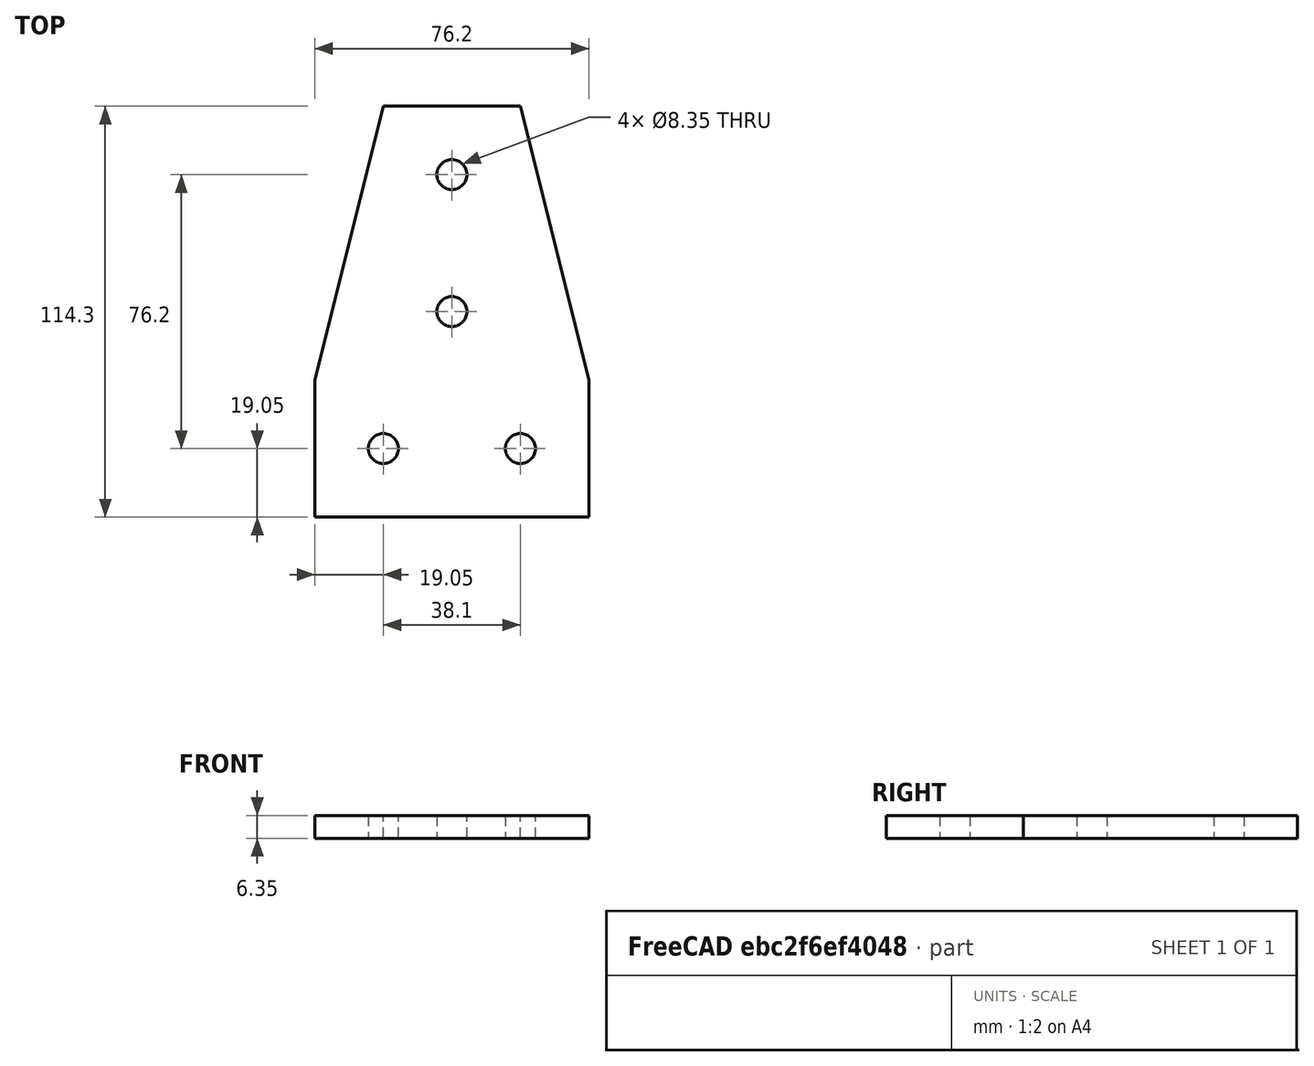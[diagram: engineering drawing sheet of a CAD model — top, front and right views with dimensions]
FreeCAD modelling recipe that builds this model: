
FCSTD DOCUMENT  (FreeCAD 0.18R)
Label: 1515-tee-plate-4
License: All rights reserved
LicenseURL: http://en.wikipedia.org/wiki/All_rights_reserved
objects: Sketcher::SketchObject×1, PartDesign::Pad×1, PartDesign::Body×1
note: 4 computed .brp shape members not serialized (recipe doc carries the construction recipe); baked Part::Feature solids carry a one-line shape summary decoded from their .brp

FEATURE [Sketcher::SketchObject] Sketch
  MapMode = 5
  Support = -> [XY_Plane]
  sketch-geometry (12):
    g0: LineSegment StartX=0 StartY=0 StartZ=0 EndX=-38.1 EndY=0 EndZ=0
    g1: LineSegment StartX=0 StartY=0 StartZ=0 EndX=38.1 EndY=0 EndZ=0
    g2: LineSegment StartX=-38.1 StartY=0 StartZ=0 EndX=-38.1 EndY=38.1 EndZ=0
    g3: LineSegment StartX=38.1 StartY=0 StartZ=0 EndX=38.1 EndY=38.1 EndZ=0
    g4: LineSegment StartX=0 StartY=114.3 StartZ=0 EndX=-19.05 EndY=114.3 EndZ=0
    g5: LineSegment StartX=0 StartY=114.3 StartZ=0 EndX=19.05 EndY=114.3 EndZ=0
    g6: LineSegment StartX=-38.1 StartY=38.1 StartZ=0 EndX=-19.05 EndY=114.3 EndZ=0
    g7: LineSegment StartX=19.05 StartY=114.3 StartZ=0 EndX=38.1 EndY=38.1 EndZ=0
    g8: Circle CenterX=-19.05 CenterY=19.05 CenterZ=0 NormalX=0 NormalY=0 NormalZ=1 AngleXU=0 Radius=4.175
    g9: Circle CenterX=19.05 CenterY=19.05 CenterZ=0 NormalX=0 NormalY=0 NormalZ=1 AngleXU=0 Radius=4.175
    g10: Circle CenterX=0 CenterY=95.25 CenterZ=0 NormalX=0 NormalY=0 NormalZ=1 AngleXU=0 Radius=4.175
    g11: Circle CenterX=0 CenterY=57.15 CenterZ=0 NormalX=0 NormalY=0 NormalZ=1 AngleXU=0 Radius=4.175
  constraints (35):
    c: Coincident(g0,g-1)
    c: PointOnObject(g0,g-1)
    c: Coincident(g1,g0)
    c: PointOnObject(g1,g-1)
    c: DistanceX(g0,g0) = 38.1
    c: Equal(g1,g0)
    c: Coincident(g2,g0)
    c: Vertical(g2)
    c: Coincident(g3,g1)
    c: Vertical(g3)
    c: Equal(g3,g2)
    c: DistanceY(g2,g2) = 38.1
    c: PointOnObject(g4,g-2)
    c: Horizontal(g4)
    c: DistanceX(g4,g4) = 19.05
    c: Coincident(g5,g4)
    c: Horizontal(g5)
    c: Equal(g5,g4)
    c: DistanceY(g0,g4) = 114.3
    c: Coincident(g6,g2)
    c: Coincident(g6,g4)
    c: Coincident(g7,g5)
    c: Coincident(g7,g3)
    c: Equal(g8,g9)
    c: Diameter(g8) = 8.35
    c: Equal(g8,g11)
    c: Equal(g8,g10)
    c: PointOnObject(g10,g-2)
    c: PointOnObject(g11,g-2)
    c: DistanceY(g8,g9) = 0
    c: DistanceX(g8,g0) = 19.05
    c: DistanceX(g0,g9) = 19.05
    c: DistanceY(g0,g8) = 19.05
    c: DistanceY(g10,g4) = 19.05
    c: DistanceY(g11,g10) = 38.1
FEATURE [PartDesign::Pad] Pad
  Length = 6.35
  Length2 = 100
  Profile = -> Sketch
  Type = 0
FEATURE [PartDesign::Body] Body  label="1515-tee-plate-4"
  Group = -> [Sketch,Pad]
  Origin = -> Origin
  Tip = -> Pad
